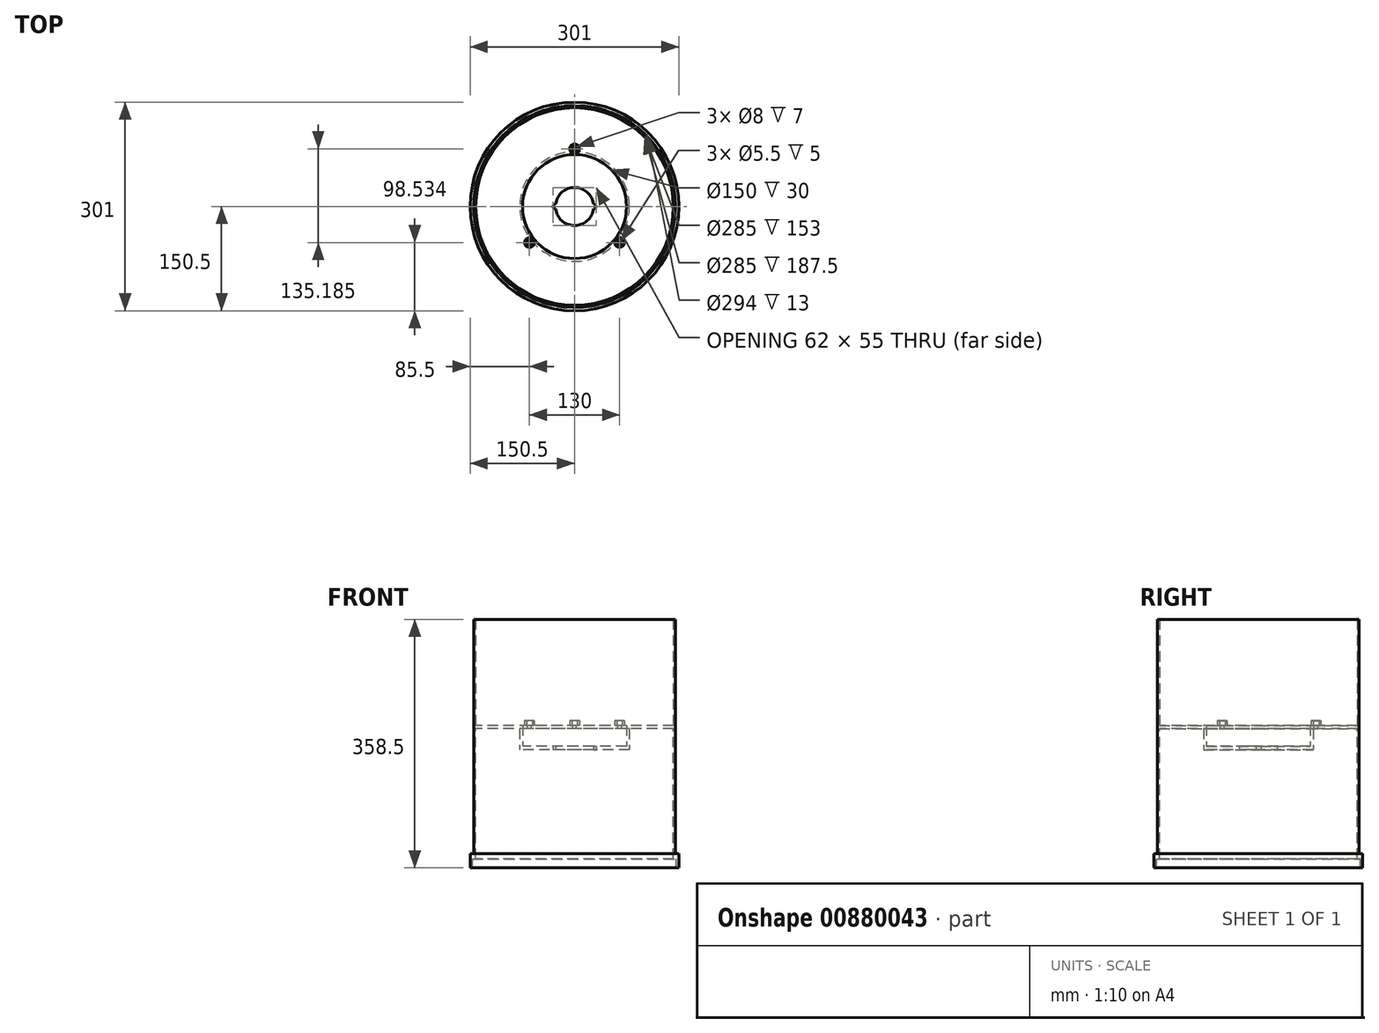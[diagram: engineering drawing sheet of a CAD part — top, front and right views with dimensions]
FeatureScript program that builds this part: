
annotation { "Feature Type Name" : "Feature", "Feature Type Description" : "" }
export const myFeature = defineFeature(function(context is Context, id is Id, definition is map)
    precondition{}
    {
        {
            var Q0;
            Q0=qCreatedBy(makeId("Top.planeOp"),FACE);
            var sketch = newSketch(context, id + "F0", { "sketchPlane" : qUnion([Q0])});
            skCircle(sketch, "E0", {"center": v(0, 0) * mm, "radius": 79 * mm});
            skArc(sketch, "E1", {"start": v(27.28, 3.5) * mm, "mid": v(0, 27.5) * mm, "end": v(-27.28, 3.5) * mm});
            skArc(sketch, "E2", {"start": v(-27.28, 3.5) * mm, "mid": v(-31, 0) * mm, "end": v(-27.28, -3.5) * mm});
            skArc(sketch, "E3", {"start": v(27.28, -3.5) * mm, "mid": v(31, 0) * mm, "end": v(27.28, 3.5) * mm});
            skArc(sketch, "E4.trimOffspring", {"start": v(-27.28, -3.5) * mm, "mid": v(0, -27.5) * mm, "end": v(27.28, -3.5) * mm});
            skCircle(sketch, "E5", {"center": v(0, 0) * mm, "radius": 75 * mm});
            skSolve(sketch);
        }
        {
            var Q0;
            Q0=makeQuery(id+"F0.imprint","IMPRINT",FACE,{"disambiguationData":[TD([[makeQuery(id+"F0.imprint","IMPRINT",EDGE,{"derivedFrom":sQuery(id+"F0.wireOp",EDGE,"E1")}),-1.0]])]});
            extrude(context, id + "F1", {"entities" : qUnion([Q0]), "depth" : 5 * mm});
        }
        {
            var Q0;
            Q0=makeQuery(id+"F0.imprint","IMPRINT",FACE,{"disambiguationData":[TD([[makeQuery(id+"F0.imprint","IMPRINT",EDGE,{"derivedFrom":sQuery(id+"F0.wireOp",EDGE,"E0")}),1.0]])]});
            extrude(context, id + "F2", {"entities" : qUnion([Q0]), "operationType" : NewBodyOperationType.ADD, "depth" : 30 * mm});
        }
        {
            var Q0;
            Q0=makeQuery(id+"F2.opExtrude","CAP_FACE",FACE,{"disambiguationData":[OSD([sQuery(id+"F0.wireOp",EDGE,"E0"),sQuery(id+"F0.wireOp",EDGE,"E5")])],"isStart":false});
            var sketch = newSketch(context, id + "F3", { "sketchPlane" : qUnion([Q0])});
            skCircle(sketch, "E6", {"center": v(0, 0) * mm, "radius": 142.5 * mm});
            skCircle(sketch, "E7.0", {"center": v(0, 0) * mm, "radius": 145.5 * mm});
            skSolve(sketch);
        }
        {
            var Q0;
            Q0=makeQuery(id+"F3.imprint","IMPRINT",FACE,{"disambiguationData":[TD([[makeQuery(id+"F3.imprint","IMPRINT",EDGE,{"derivedFrom":sQuery(id+"F3.wireOp",EDGE,"E6")}),1.0]])]});
            var Q1;
            Q1=makeQuery(id+"F3.imprint","IMPRINT",FACE,{"disambiguationData":[TD([[makeQuery(id+"F3.imprint","IMPRINT",EDGE,{"derivedFrom":makeQuery(id+"F2.opExtrude","CAP_EDGE",EDGE,{"disambiguationData":[OSD([sQuery(id+"F0.wireOp",EDGE,"E0")])],"isStart":false})}),1.0]])]});
            extrude(context, id + "F4", {"entities" : qUnion([Q0, Q1]), "operationType" : NewBodyOperationType.ADD, "depth" : 5 * mm});
        }
        {
            var Q0;
            Q0=makeQuery(id+"F3.imprint","IMPRINT",FACE,{"disambiguationData":[TD([[makeQuery(id+"F3.imprint","IMPRINT",EDGE,{"derivedFrom":sQuery(id+"F3.wireOp",EDGE,"E6")}),-1.0]])]});
            extrude(context, id + "F5", {"entities" : qUnion([Q0]), "operationType" : NewBodyOperationType.ADD, "depth" : 158 * mm});
        }
        {
            var Q0;
            Q0=makeQuery(id+"F3.imprint","IMPRINT",FACE,{"disambiguationData":[TD([[makeQuery(id+"F3.imprint","IMPRINT",EDGE,{"derivedFrom":sQuery(id+"F3.wireOp",EDGE,"E6")}),-1.0]])]});
            extrude(context, id + "F6", {"entities" : qUnion([Q0]), "operationType" : NewBodyOperationType.ADD, "oppositeDirection" : true, "depth" : 180 * mm});
        }
        {
            var Q0;
            Q0=makeQuery(id+"F6.opExtrude","CAP_FACE",FACE,{"disambiguationData":[OSD([sQuery(id+"F3.wireOp",EDGE,"E6"),sQuery(id+"F3.wireOp",EDGE,"E7.0")])],"isStart":false});
            var sketch = newSketch(context, id + "F7", { "sketchPlane" : qUnion([Q0])});
            skCircle(sketch, "E8", {"center": v(0, 0) * mm, "radius": 150.5 * mm});
            skSolve(sketch);
        }
        {
            var Q0;
            Q0=makeQuery(id+"F7.imprint","IMPRINT",FACE,{"disambiguationData":[TD([[makeQuery(id+"F7.imprint","IMPRINT",EDGE,{"derivedFrom":sQuery(id+"F7.wireOp",EDGE,"E8")}),1.0]])]});
            var Q1;
            Q1=makeQuery(id+"F7.imprint","IMPRINT",FACE,{"disambiguationData":[TD([[makeQuery(id+"F7.imprint","IMPRINT",EDGE,{"derivedFrom":makeQuery(id+"F6.opExtrude","CAP_EDGE",EDGE,{"disambiguationData":[OSD([sQuery(id+"F3.wireOp",EDGE,"E6")])],"isStart":false})}),1.0]])]});
            extrude(context, id + "F8", {"entities" : qUnion([Q0, Q1]), "operationType" : NewBodyOperationType.ADD, "depth" : 7.5 * mm});
        }
        {
            var Q0;
            Q0=makeQuery(id+"F8.opExtrude","CAP_FACE",FACE,{"disambiguationData":[OSD([sQuery(id+"F3.wireOp",EDGE,"E6"),sQuery(id+"F7.wireOp",EDGE,"E8")])],"isStart":false});
            var sketch = newSketch(context, id + "F9", { "sketchPlane" : qUnion([Q0])});
            skCircle(sketch, "E9", {"center": v(0, 0) * mm, "radius": 147 * mm});
            skSolve(sketch);
        }
        {
            var Q0;
            Q0=makeQuery(id+"F9.imprint","IMPRINT",FACE,{"disambiguationData":[TD([[makeQuery(id+"F9.imprint","IMPRINT",EDGE,{"derivedFrom":sQuery(id+"F9.wireOp",EDGE,"E9")}),-1.0]])]});
            extrude(context, id + "F10", {"entities" : qUnion([Q0]), "operationType" : NewBodyOperationType.ADD, "depth" : 13 * mm});
        }
        {
            var Q0;
            Q0=makeQuery(id+"F4.opExtrude","CAP_FACE",FACE,{"disambiguationData":[OSD([sQuery(id+"F0.wireOp",EDGE,"E5"),sQuery(id+"F3.wireOp",EDGE,"E6")])],"isStart":false});
            var sketch = newSketch(context, id + "F11", { "sketchPlane" : qUnion([Q0])});
            skCircle(sketch, "E10", {"center": v(0, 83.22) * mm, "radius": 4 * mm});
            skCircle(sketch, "E11.0", {"center": v(0, 83.22) * mm, "radius": 7 * mm});
            skCircle(sketch, "E12", {"center": v(0, 83.22) * mm, "radius": 2.5 * mm});
            skCircle(sketch, "E13.1.0", {"center": v(-65, -51.97) * mm, "radius": 2.5 * mm});
            skCircle(sketch, "E13.1.1", {"center": v(-65, -51.97) * mm, "radius": 7 * mm});
            skCircle(sketch, "E13.1.2", {"center": v(-65, -51.97) * mm, "radius": 4 * mm});
            skCircle(sketch, "E13.2.0", {"center": v(65, -51.97) * mm, "radius": 2.5 * mm});
            skCircle(sketch, "E13.2.1", {"center": v(65, -51.97) * mm, "radius": 7 * mm});
            skCircle(sketch, "E13.2.2", {"center": v(65, -51.97) * mm, "radius": 4 * mm});
            skPoint(sketch, "E13.center", {"position": v(0, 0) * mm});
            skCircle(sketch, "E14", {"center": v(0, 0) * mm, "radius": 83.22 * mm, "construction": true});
            skSolve(sketch);
        }
        {
            var Q0;
            Q0=makeQuery(id+"F11.imprint","IMPRINT",FACE,{"disambiguationData":[TD([[makeQuery(id+"F11.imprint","IMPRINT",EDGE,{"derivedFrom":sQuery(id+"F11.wireOp",EDGE,"E10")}),-1.0]])]});
            var Q1;
            Q1=makeQuery(id+"F11.imprint","IMPRINT",FACE,{"disambiguationData":[TD([[makeQuery(id+"F11.imprint","IMPRINT",EDGE,{"derivedFrom":sQuery(id+"F11.wireOp",EDGE,"E13.1.1")}),1.0]])]});
            var Q2;
            Q2=makeQuery(id+"F11.imprint","IMPRINT",FACE,{"disambiguationData":[TD([[makeQuery(id+"F11.imprint","IMPRINT",EDGE,{"derivedFrom":sQuery(id+"F11.wireOp",EDGE,"E13.2.1")}),1.0]])]});
            extrude(context, id + "F12", {"entities" : qUnion([Q0, Q1, Q2]), "operationType" : NewBodyOperationType.ADD, "depth" : 7 * mm});
        }
        {
            var Q0;
            Q0=sQuery(id+"F11.wireOp",VERTEX,"E10.center");
            var Q1;
            Q1=sQuery(id+"F11.wireOp",VERTEX,"E13.1.0.center");
            var Q2;
            Q2=sQuery(id+"F11.wireOp",VERTEX,"E13.2.0.center");
            var Q3;
            Q3=makeQuery(id+"F1.opExtrude","SWEPT_BODY",BODY,{"disambiguationData":[OSD([sQuery(id+"F0.wireOp",EDGE,"E1"),sQuery(id+"F0.wireOp",EDGE,"E2"),sQuery(id+"F0.wireOp",EDGE,"E3"),sQuery(id+"F0.wireOp",EDGE,"E4.trimOffspring"),sQuery(id+"F0.wireOp",EDGE,"E5")])]});
            hole(context, id + "F13", {"style" : HoleStyle.SIMPLE, "endStyle" : HoleEndStyle.BLIND, "standardTappedOrClearance" : lookupTablePath({ "standard" : "ISO", "fit" : "Normal", "size" : "M5", "type" : "Clearance" }), "standardBlindInLast" : lookupTablePath({ "fit" : "Standard", "standard" : "ISO", "size" : "M5", "type" : "Clearance" }), "holeDiameter" : 5.5 * mm, "holeDepth" : 12 * mm, "locations" : qUnion([Q0, Q1, Q2]), "scope" : qUnion([Q3])});
        }
    });
